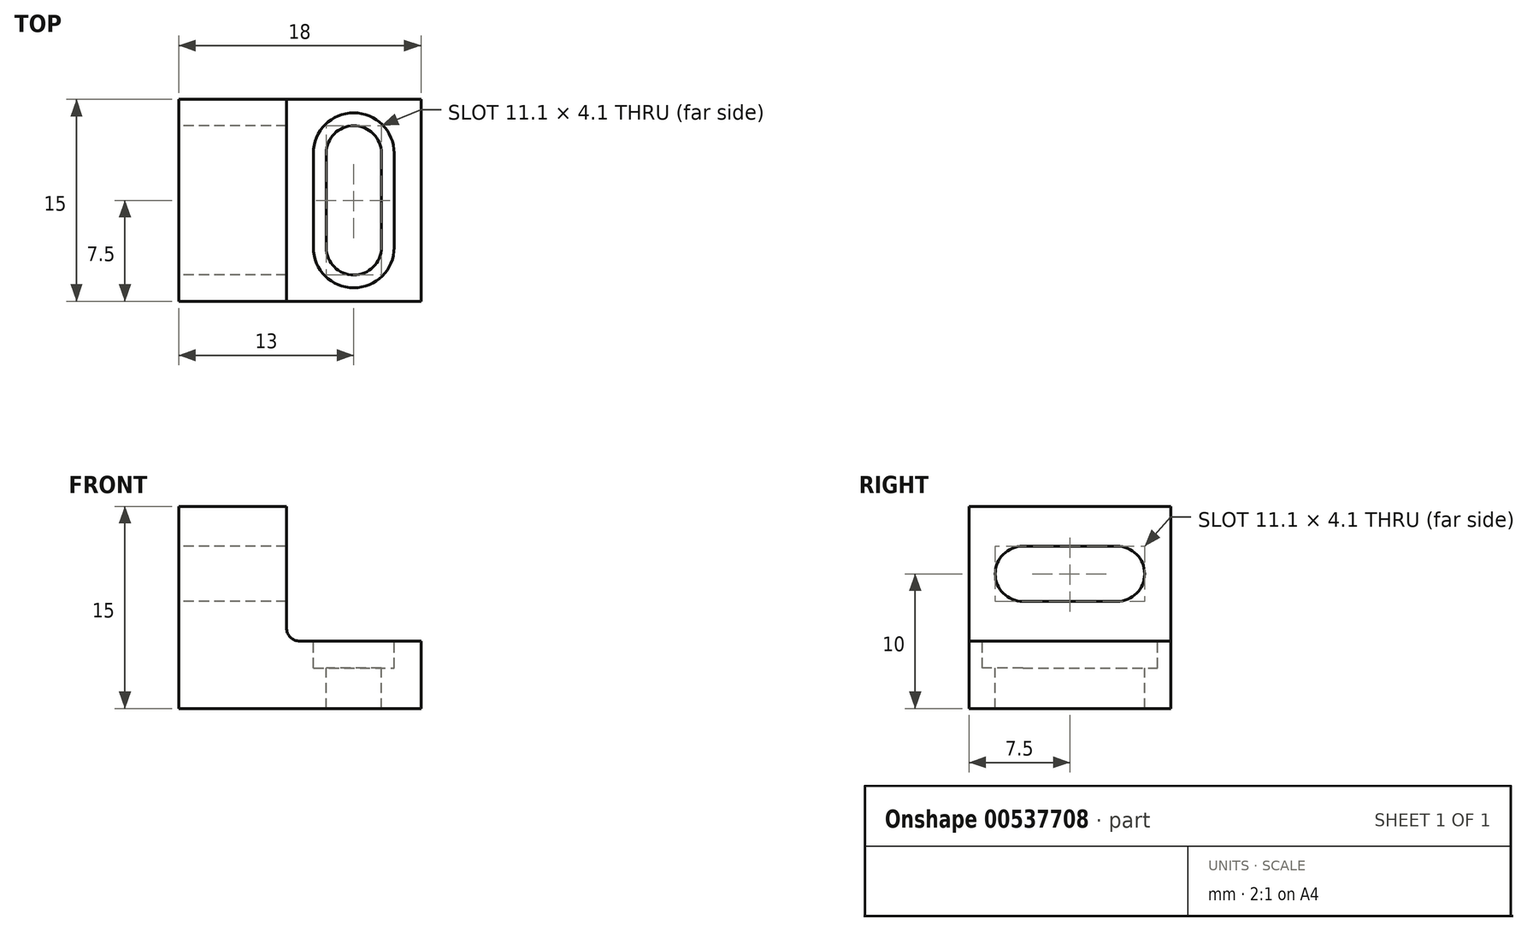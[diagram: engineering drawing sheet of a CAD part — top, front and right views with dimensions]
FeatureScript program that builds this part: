
annotation { "Feature Type Name" : "Feature", "Feature Type Description" : "" }
export const myFeature = defineFeature(function(context is Context, id is Id, definition is map)
    precondition{}
    {
        {
            var Q0;
            Q0=qCreatedBy(makeId("Top.planeOp"),FACE);
            var sketch = newSketch(context, id + "F0", { "sketchPlane" : qUnion([Q0])});
            skLineSegment(sketch, "E0.bottom", {"start": v(0, 0) * mm, "end": v(18, 0) * mm});
            skLineSegment(sketch, "E0.top", {"start": v(0, 15) * mm, "end": v(18, 15) * mm});
            skLineSegment(sketch, "E0.left", {"start": v(0, 0) * mm, "end": v(0, 15) * mm});
            skLineSegment(sketch, "E0.right", {"start": v(18, 0) * mm, "end": v(18, 15) * mm});
            skSolve(sketch);
        }
        {
            var Q0;
            Q0 = qSketchRegion(id + "F0", true);
            extrude(context, id + "F1", {"entities" : qUnion([Q0]), "depth" : 15 * mm, "offsetDistance" : 25 * mm});
        }
        {
            var Q0;
            Q0=makeQuery(id+"F1.opExtrude","SWEPT_FACE",FACE,{"disambiguationData":[OSD([sQuery(id+"F0.wireOp",EDGE,"E0.left")])]});
            var sketch = newSketch(context, id + "F2", { "sketchPlane" : qUnion([Q0])});
            skArc(sketch, "E1", {"start": v(-4, 7.95) * mm, "mid": v(-1.95, 10) * mm, "end": v(-4, 12.05) * mm});
            skArc(sketch, "E2", {"start": v(-11, 12.05) * mm, "mid": v(-13.05, 10) * mm, "end": v(-11, 7.95) * mm});
            skLineSegment(sketch, "E3", {"start": v(-11, 12.05) * mm, "end": v(-4, 12.05) * mm});
            skLineSegment(sketch, "E4", {"start": v(-4, 7.95) * mm, "end": v(-11, 7.95) * mm});
            skSolve(sketch);
        }
        {
            var Q0;
            Q0 = qSketchRegion(id + "F2", true);
            extrude(context, id + "F3", {"entities" : qUnion([Q0]), "operationType" : NewBodyOperationType.REMOVE, "oppositeDirection" : true, "depth" : 25 * mm, "offsetDistance" : 25 * mm});
        }
        {
            var Q0;
            Q0=makeQuery(id+"F1.opExtrude","CAP_FACE",FACE,{"disambiguationData":[OSD([sQuery(id+"F0.wireOp",EDGE,"E0.bottom"),sQuery(id+"F0.wireOp",EDGE,"E0.top"),sQuery(id+"F0.wireOp",EDGE,"E0.left"),sQuery(id+"F0.wireOp",EDGE,"E0.right")])],"isStart":false});
            var sketch = newSketch(context, id + "F4", { "sketchPlane" : qUnion([Q0])});
            skLineSegment(sketch, "E5.bottom", {"start": v(18, 15) * mm, "end": v(8, 15) * mm});
            skLineSegment(sketch, "E5.top", {"start": v(18, 0) * mm, "end": v(8, 0) * mm});
            skLineSegment(sketch, "E5.left", {"start": v(18, 15) * mm, "end": v(18, 0) * mm});
            skLineSegment(sketch, "E5.right", {"start": v(8, 15) * mm, "end": v(8, 0) * mm});
            skSolve(sketch);
        }
        {
            var Q0;
            Q0 = qSketchRegion(id + "F4", true);
            extrude(context, id + "F5", {"entities" : qUnion([Q0]), "operationType" : NewBodyOperationType.REMOVE, "oppositeDirection" : true, "depth" : 10 * mm, "offsetDistance" : 25 * mm});
        }
        {
            var Q0;
            Q0=makeQuery(id+"F5.boolean.opBoolean","COPY",FACE,{"derivedFrom":makeQuery(id+"F5.opExtrude","CAP_FACE",FACE,{"disambiguationData":[OSD([sQuery(id+"F4.wireOp",EDGE,"E5.bottom"),sQuery(id+"F4.wireOp",EDGE,"E5.top"),sQuery(id+"F4.wireOp",EDGE,"E5.left"),sQuery(id+"F4.wireOp",EDGE,"E5.right")])],"isStart":false})});
            var sketch = newSketch(context, id + "F6", { "sketchPlane" : qUnion([Q0])});
            skArc(sketch, "E6", {"start": v(15.05, 11) * mm, "mid": v(13, 13.05) * mm, "end": v(10.95, 11) * mm});
            skArc(sketch, "E7", {"start": v(10.95, 4) * mm, "mid": v(13, 1.95) * mm, "end": v(15.05, 4) * mm});
            skLineSegment(sketch, "E8", {"start": v(10.95, 11) * mm, "end": v(10.95, 4) * mm});
            skLineSegment(sketch, "E9", {"start": v(15.05, 11) * mm, "end": v(15.05, 4) * mm});
            skSolve(sketch);
        }
        {
            var Q0;
            Q0 = qSketchRegion(id + "F6", true);
            extrude(context, id + "F7", {"entities" : qUnion([Q0]), "operationType" : NewBodyOperationType.REMOVE, "oppositeDirection" : true, "depth" : 25 * mm, "offsetDistance" : 25 * mm});
        }
        {
            var Q0;
            Q0=makeQuery(id+"F5.boolean.opBoolean","COPY",FACE,{"derivedFrom":makeQuery(id+"F5.opExtrude","CAP_FACE",FACE,{"disambiguationData":[OSD([sQuery(id+"F4.wireOp",EDGE,"E5.bottom"),sQuery(id+"F4.wireOp",EDGE,"E5.top"),sQuery(id+"F4.wireOp",EDGE,"E5.left"),sQuery(id+"F4.wireOp",EDGE,"E5.right")])],"isStart":false})});
            var sketch = newSketch(context, id + "F8", { "sketchPlane" : qUnion([Q0])});
            skArc(sketch, "E10", {"start": v(16, 11) * mm, "mid": v(13, 14) * mm, "end": v(10, 11) * mm});
            skArc(sketch, "E11", {"start": v(10, 4) * mm, "mid": v(13, 1) * mm, "end": v(16, 4) * mm});
            skLineSegment(sketch, "E12.left", {"start": v(10, 4) * mm, "end": v(10, 11) * mm});
            skLineSegment(sketch, "E12.right", {"start": v(16, 4) * mm, "end": v(16, 11) * mm});
            skSolve(sketch);
        }
        {
            var Q0;
            Q0 = qSketchRegion(id + "F8", true);
            extrude(context, id + "F9", {"entities" : qUnion([Q0]), "operationType" : NewBodyOperationType.REMOVE, "oppositeDirection" : true, "depth" : 2 * mm, "offsetDistance" : 25 * mm});
        }
        {
            var Q0;
            Q0=makeQuery(id+"F5.boolean.opBoolean","COPY",EDGE,{"derivedFrom":makeQuery(id+"F5.opExtrude","CAP_EDGE",EDGE,{"disambiguationData":[OSD([sQuery(id+"F4.wireOp",EDGE,"E5.right")])],"isStart":false})});
            fillet(context, id + "F10", {"entities" : qUnion([Q0]), "radius" : 1 * mm, "tangentPropagation" : true, "allowEdgeOverflow" : false});
        }
    });
